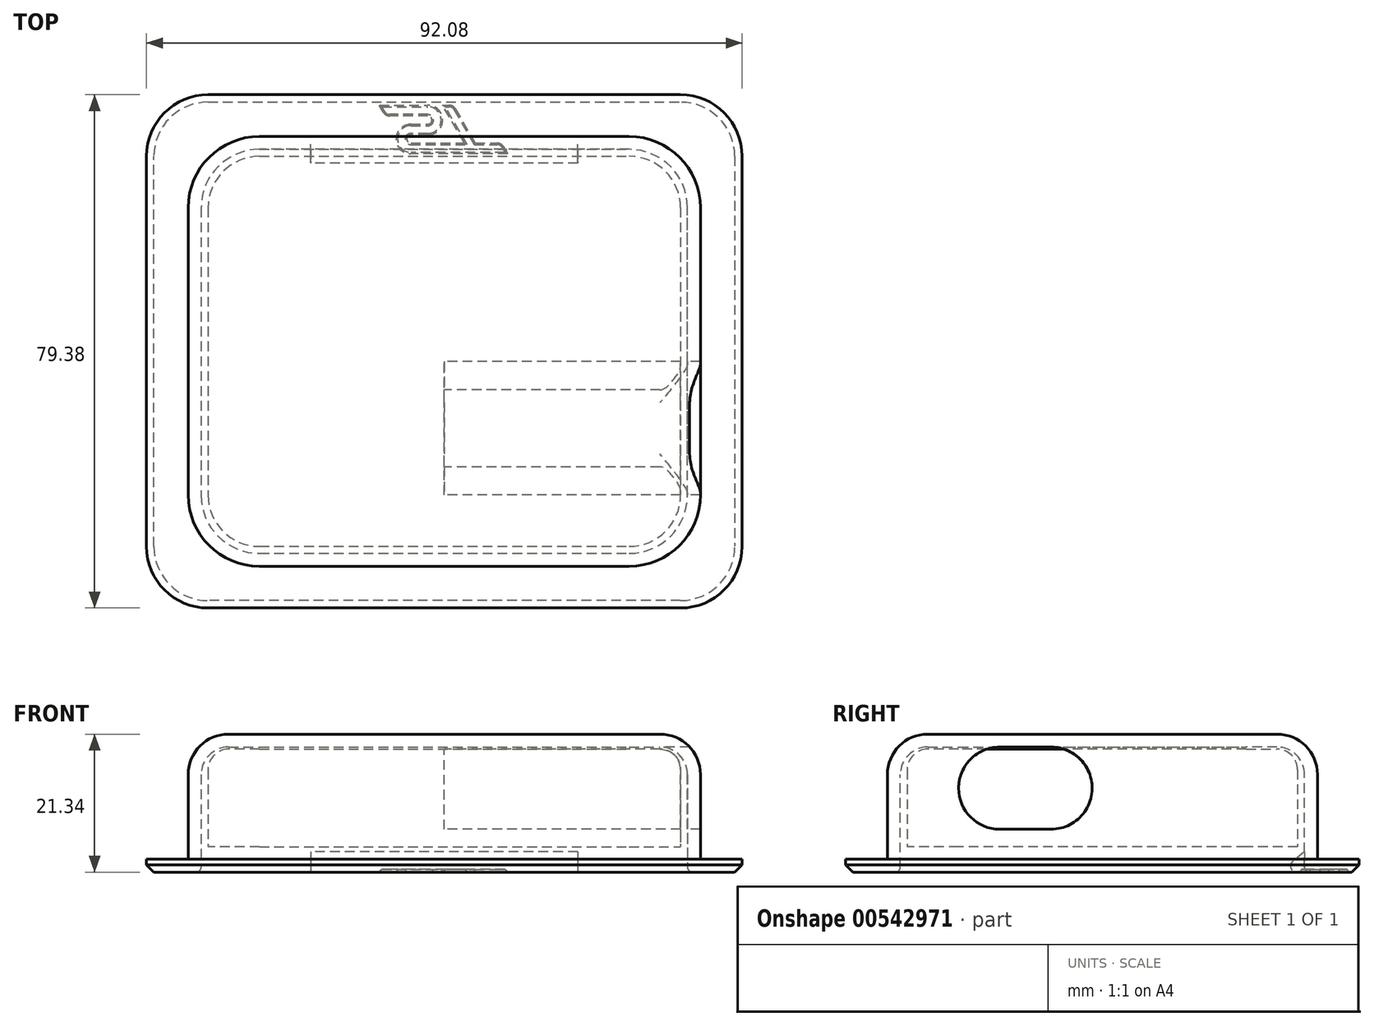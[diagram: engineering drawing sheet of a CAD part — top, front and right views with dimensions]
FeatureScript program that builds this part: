
annotation { "Feature Type Name" : "Feature", "Feature Type Description" : "" }
export const myFeature = defineFeature(function(context is Context, id is Id, definition is map)
    precondition{}
    {
        {
            var Q0;
            Q0=qCreatedBy(makeId("Top.planeOp"),FACE);
            var sketch = newSketch(context, id + "F0", { "sketchPlane" : qUnion([Q0])});
            skLineSegment(sketch, "E0.bottom", {"start": v(-28.58, 30.16) * mm, "end": v(28.58, 30.16) * mm});
            skLineSegment(sketch, "E0.top", {"start": v(-28.58, -30.16) * mm, "end": v(28.58, -30.16) * mm});
            skLineSegment(sketch, "E0.left", {"start": v(-36.51, 22.23) * mm, "end": v(-36.51, -22.23) * mm});
            skLineSegment(sketch, "E0.right", {"start": v(36.51, 22.23) * mm, "end": v(36.51, -22.23) * mm});
            skLineSegment(sketch, "E1", {"start": v(0, 30.16) * mm, "end": v(0, -30.16) * mm, "construction": true});
            skPoint(sketch, "E2.visualSharp", {"position": v(-36.51, 30.16) * mm});
            skArc(sketch, "E2.filletArc", {"start": v(-28.58, 30.16) * mm, "mid": v(-34.19, 27.84) * mm, "end": v(-36.51, 22.23) * mm});
            skPoint(sketch, "E3.visualSharp", {"position": v(-36.51, -30.16) * mm});
            skArc(sketch, "E3.filletArc", {"start": v(-36.51, -22.23) * mm, "mid": v(-34.19, -27.84) * mm, "end": v(-28.58, -30.16) * mm});
            skPoint(sketch, "E4.visualSharp", {"position": v(36.51, 30.16) * mm});
            skArc(sketch, "E4.filletArc", {"start": v(36.51, 22.23) * mm, "mid": v(34.19, 27.84) * mm, "end": v(28.58, 30.16) * mm});
            skPoint(sketch, "E5.visualSharp", {"position": v(36.51, -30.16) * mm});
            skArc(sketch, "E5.filletArc", {"start": v(28.58, -30.16) * mm, "mid": v(34.19, -27.84) * mm, "end": v(36.51, -22.22) * mm});
            skSolve(sketch);
        }
        {
            var Q0;
            Q0 = qSketchRegion(id + "F0", true);
            extrude(context, id + "F1", {"entities" : qUnion([Q0]), "depth" : 18.26 * mm, "offsetDistance" : 25.4 * mm});
        }
        {
            var Q0;
            Q0=makeQuery(id+"F1.opExtrude","CAP_EDGE",EDGE,{"disambiguationData":[OSD([sQuery(id+"F0.wireOp",EDGE,"E0.right")])],"isStart":true});
            var Q1;
            Q1=makeQuery(id+"F1.opExtrude","CAP_FACE",FACE,{"disambiguationData":[OSD([sQuery(id+"F0.wireOp",EDGE,"E0.bottom"),sQuery(id+"F0.wireOp",EDGE,"E0.top"),sQuery(id+"F0.wireOp",EDGE,"E0.left"),sQuery(id+"F0.wireOp",EDGE,"E0.right"),sQuery(id+"F0.wireOp",EDGE,"E2.filletArc"),sQuery(id+"F0.wireOp",EDGE,"E3.filletArc"),sQuery(id+"F0.wireOp",EDGE,"E4.filletArc"),sQuery(id+"F0.wireOp",EDGE,"E5.filletArc")])],"isStart":false});
            fillet(context, id + "F2", {"entities" : qUnion([Q0, Q1]), "radius" : 3.17 * mm, "tangentPropagation" : true, "allowEdgeOverflow" : false});
        }
        {
            var Q0;
            Q0=makeQuery(id+"F1.opExtrude","CAP_FACE",FACE,{"disambiguationData":[OSD([sQuery(id+"F0.wireOp",EDGE,"E0.bottom"),sQuery(id+"F0.wireOp",EDGE,"E0.top"),sQuery(id+"F0.wireOp",EDGE,"E0.left"),sQuery(id+"F0.wireOp",EDGE,"E0.right"),sQuery(id+"F0.wireOp",EDGE,"E2.filletArc"),sQuery(id+"F0.wireOp",EDGE,"E3.filletArc"),sQuery(id+"F0.wireOp",EDGE,"E4.filletArc"),sQuery(id+"F0.wireOp",EDGE,"E5.filletArc")])],"isStart":false});
            var sketch = newSketch(context, id + "F3", { "sketchPlane" : qUnion([Q0])});
            skCircle(sketch, "E6", {"center": v(0, 1.94) * mm, "radius": 1.78 * mm});
            skSolve(sketch);
        }
        {
            var Q0;
            Q0=qCreatedBy(makeId("Top.planeOp"),FACE);
            cPlane(context, id + "F4", {"entities" : qUnion([Q0]), "cplaneType" : CPlaneType.OFFSET, "offset" : 50.8 * mm, "width" : 152.4 * mm, "height" : 152.4 * mm});
        }
        {
            var Q0;
            Q0=qCreatedBy(id+"F4.planeOp",FACE);
            var sketch = newSketch(context, id + "F5", { "sketchPlane" : qUnion([Q0])});
            skLineSegment(sketch, "E7.bottom", {"start": v(-46.04, 39.69) * mm, "end": v(46.04, 39.69) * mm});
            skLineSegment(sketch, "E7.top", {"start": v(-46.04, -39.69) * mm, "end": v(46.04, -39.69) * mm});
            skLineSegment(sketch, "E7.left", {"start": v(-46.04, 39.69) * mm, "end": v(-46.04, -39.69) * mm});
            skLineSegment(sketch, "E7.right", {"start": v(46.04, 39.69) * mm, "end": v(46.04, -39.69) * mm});
            skLineSegment(sketch, "E8", {"start": v(0, 39.69) * mm, "end": v(0, -39.69) * mm, "construction": true});
            skLineSegment(sketch, "E9.0", {"start": v(-28.58, 30.16) * mm, "end": v(28.58, 30.16) * mm, "construction": true});
            skArc(sketch, "E9.1", {"start": v(28.58, 30.16) * mm, "mid": v(34.19, 27.84) * mm, "end": v(36.51, 22.23) * mm, "construction": true});
            skLineSegment(sketch, "E9.2", {"start": v(36.51, 22.23) * mm, "end": v(36.51, -22.23) * mm, "construction": true});
            skArc(sketch, "E9.3", {"start": v(36.51, -22.23) * mm, "mid": v(34.19, -27.84) * mm, "end": v(28.58, -30.16) * mm, "construction": true});
            skLineSegment(sketch, "E9.4", {"start": v(28.58, -30.16) * mm, "end": v(-28.58, -30.16) * mm, "construction": true});
            skArc(sketch, "E9.5", {"start": v(-28.58, -30.16) * mm, "mid": v(-34.19, -27.84) * mm, "end": v(-36.51, -22.23) * mm, "construction": true});
            skLineSegment(sketch, "E9.6", {"start": v(-36.51, -22.23) * mm, "end": v(-36.51, 22.23) * mm, "construction": true});
            skArc(sketch, "E9.7", {"start": v(-36.51, 22.23) * mm, "mid": v(-34.19, 27.84) * mm, "end": v(-28.58, 30.16) * mm, "construction": true});
            skSolve(sketch);
        }
        {
            var Q0;
            Q0 = qSketchRegion(id + "F5", true);
            extrude(context, id + "F6", {"entities" : qUnion([Q0]), "depth" : 22.22 * mm, "offsetDistance" : 25.4 * mm});
        }
        {
            var Q0;
            Q0=makeQuery(id+"F1.opExtrude","SWEPT_BODY",BODY,{"disambiguationData":[OSD([sQuery(id+"F0.wireOp",EDGE,"E0.bottom"),sQuery(id+"F0.wireOp",EDGE,"E0.top"),sQuery(id+"F0.wireOp",EDGE,"E0.left"),sQuery(id+"F0.wireOp",EDGE,"E0.right"),sQuery(id+"F0.wireOp",EDGE,"E2.filletArc"),sQuery(id+"F0.wireOp",EDGE,"E3.filletArc"),sQuery(id+"F0.wireOp",EDGE,"E4.filletArc"),sQuery(id+"F0.wireOp",EDGE,"E5.filletArc")])]});
            transform(context, id + "F7", {"entities" : qUnion([Q0]), "transformType" : TransformType.TRANSLATION_3D, "dx" : 0 * mm, "dy" : 0 * mm, "dz" : 50.8 * mm, "makeCopy" : false});
        }
        {
            var Q0;
            Q0=makeQuery(id+"F1.opExtrude","SWEPT_BODY",BODY,{"disambiguationData":[OSD([sQuery(id+"F0.wireOp",EDGE,"E0.bottom"),sQuery(id+"F0.wireOp",EDGE,"E0.top"),sQuery(id+"F0.wireOp",EDGE,"E0.left"),sQuery(id+"F0.wireOp",EDGE,"E0.right"),sQuery(id+"F0.wireOp",EDGE,"E2.filletArc"),sQuery(id+"F0.wireOp",EDGE,"E3.filletArc"),sQuery(id+"F0.wireOp",EDGE,"E4.filletArc"),sQuery(id+"F0.wireOp",EDGE,"E5.filletArc")])]});
            var Q1;
            Q1=makeQuery(id+"F6.opExtrude","SWEPT_BODY",BODY,{"disambiguationData":[OSD([sQuery(id+"F5.wireOp",EDGE,"E7.bottom"),sQuery(id+"F5.wireOp",EDGE,"E7.top"),sQuery(id+"F5.wireOp",EDGE,"E7.left"),sQuery(id+"F5.wireOp",EDGE,"E7.right")])]});
            booleanBodies(context, id + "F8", {"operationType" : BooleanOperationType.SUBTRACTION, "tools" : qUnion([Q0]), "targets" : qUnion([Q1]), "offset" : true, "offsetAll" : true, "offsetDistance" : 1.08 * mm, "keepTools" : true});
        }
        {
            var Q0;
            Q0=qCreatedBy(id+"F4.planeOp",FACE);
            var Q1;
            {var subQ0=sQuery(id+"F0.wireOp",EDGE,"E2.filletArc");var subQ1=sQuery(id+"F0.wireOp",EDGE,"E0.left");Q1=makeQuery(id+"F8.tempBoolean.opBoolean","COPY",VERTEX,{"derivedFrom":makeQuery(id+"F8.offsetTempBody.opPattern","COPY",VERTEX,{"derivedFrom":makeQuery(id+"F2.opFillet","BLEND_VERTEX",VERTEX,{"blendedFrom":[makeQuery(id+"F1.opExtrude","CAP_EDGE",EDGE,{"disambiguationData":[OSD([subQ1])],"isStart":true}),makeQuery(id+"F1.opExtrude","CAP_EDGE",EDGE,{"disambiguationData":[OSD([subQ0])],"isStart":true}),makeQuery(id+"F1.opExtrude","SWEPT_FACE",FACE,{"disambiguationData":[OSD([subQ1])]}),makeQuery(id+"F1.opExtrude","SWEPT_FACE",FACE,{"disambiguationData":[OSD([subQ0])]})],"blendedInto":[makeQuery(id+"F1.opExtrude","SWEPT_FACE",FACE,{"disambiguationData":[OSD([subQ1])]}),makeQuery(id+"F1.opExtrude","SWEPT_FACE",FACE,{"disambiguationData":[OSD([subQ0])]})]}),"instanceName":"1"})});}
            cPlane(context, id + "F9", {"entities" : qUnion([Q0, Q1]), "cplaneType" : CPlaneType.PLANE_POINT, "offset" : 25.4 * mm, "width" : 152.4 * mm, "height" : 152.4 * mm});
        }
        {
            var Q0;
            Q0=qCreatedBy(id+"F9.planeOp",FACE);
            var sketch = newSketch(context, id + "F10", { "sketchPlane" : qUnion([Q0])});
            skArc(sketch, "E10.0", {"start": v(28.58, -31.24) * mm, "mid": v(34.95, -28.6) * mm, "end": v(37.6, -22.22) * mm});
            skLineSegment(sketch, "E10.1", {"start": v(37.6, -22.22) * mm, "end": v(37.6, 22.23) * mm});
            skArc(sketch, "E10.2", {"start": v(37.6, 22.23) * mm, "mid": v(34.95, 28.6) * mm, "end": v(28.58, 31.24) * mm});
            skLineSegment(sketch, "E10.3", {"start": v(-28.58, -31.24) * mm, "end": v(28.58, -31.24) * mm});
            skLineSegment(sketch, "E10.4", {"start": v(28.58, 31.24) * mm, "end": v(-28.58, 31.24) * mm});
            skArc(sketch, "E10.5", {"start": v(-28.58, 31.24) * mm, "mid": v(-34.95, 28.6) * mm, "end": v(-37.6, 22.23) * mm});
            skLineSegment(sketch, "E10.6", {"start": v(-37.6, 22.23) * mm, "end": v(-37.6, -22.23) * mm});
            skArc(sketch, "E10.7", {"start": v(-37.6, -22.23) * mm, "mid": v(-34.95, -28.6) * mm, "end": v(-28.58, -31.24) * mm});
            skSolve(sketch);
        }
        {
            var Q0;
            Q0 = qSketchRegion(id + "F10", true);
            var Q1;
            Q1=makeQuery(id+"F6.opExtrude","CAP_FACE",FACE,{"disambiguationData":[OSD([sQuery(id+"F5.wireOp",EDGE,"E7.bottom"),sQuery(id+"F5.wireOp",EDGE,"E7.top"),sQuery(id+"F5.wireOp",EDGE,"E7.left"),sQuery(id+"F5.wireOp",EDGE,"E7.right")])],"isStart":true});
            extrude(context, id + "F11", {"entities" : qUnion([Q0]), "operationType" : NewBodyOperationType.REMOVE, "endBound" : BoundingType.THROUGH_ALL, "oppositeDirection" : true, "depth" : 25.4 * mm, "endBoundEntityFace" : qUnion([Q1]), "offsetDistance" : 25.4 * mm});
        }
        {
            var Q0;
            Q0=makeQuery(id+"F6.opExtrude","SWEPT_FACE",FACE,{"disambiguationData":[OSD([sQuery(id+"F5.wireOp",EDGE,"E7.bottom")])]});
            var Q1;
            Q1=makeQuery(id+"F6.opExtrude","CAP_FACE",FACE,{"disambiguationData":[OSD([sQuery(id+"F5.wireOp",EDGE,"E7.bottom"),sQuery(id+"F5.wireOp",EDGE,"E7.top"),sQuery(id+"F5.wireOp",EDGE,"E7.left"),sQuery(id+"F5.wireOp",EDGE,"E7.right")])],"isStart":false});
            var Q2;
            Q2=makeQuery(id+"F6.opExtrude","SWEPT_FACE",FACE,{"disambiguationData":[OSD([sQuery(id+"F5.wireOp",EDGE,"E7.left")])]});
            var Q3;
            Q3=makeQuery(id+"F6.opExtrude","SWEPT_FACE",FACE,{"disambiguationData":[OSD([sQuery(id+"F5.wireOp",EDGE,"E7.top")])]});
            var Q4;
            Q4=makeQuery(id+"F6.opExtrude","SWEPT_FACE",FACE,{"disambiguationData":[OSD([sQuery(id+"F5.wireOp",EDGE,"E7.right")])]});
            shell(context, id + "F12", {"entities" : qUnion([Q0, Q1, Q2, Q3, Q4]), "thickness" : 2 * mm});
        }
        {
            var Q0;
            Q0=makeQuery(id+"F20.opExtrude","CAP_EDGE",EDGE,{"disambiguationData":[OSD([sQuery(id+"F19.wireOp",EDGE,"3854df1f-5eea-4c8c-9dfc-7f40932c4ef70.MirrorCS")])],"isStart":true});
            var Q1;
            Q1=makeQuery(id+"F20.opExtrude","CAP_EDGE",EDGE,{"disambiguationData":[OSD([sQuery(id+"F19.wireOp",EDGE,"3854df1f-5eea-4c8c-9dfc-7f40932c4ef70.MirrorCS")])],"isStart":false});
            var Q2;
            Q2=makeQuery(id+"F20.opExtrude","CAP_EDGE",EDGE,{"disambiguationData":[OSD([sQuery(id+"F19.wireOp",EDGE,"E47")])],"isStart":false});
            var Q3;
            Q3=makeQuery(id+"F20.opExtrude","CAP_EDGE",EDGE,{"disambiguationData":[OSD([sQuery(id+"F19.wireOp",EDGE,"E47")])],"isStart":true});
            var Q4;
            {var subQ0=makeQuery(id+"F11.opExtrude","SWEPT_FACE",FACE,{"disambiguationData":[OSD([sQuery(id+"F10.wireOp",EDGE,"E10.3")])]});var subQ1=makeQuery(id+"F6.opExtrude","CAP_FACE",FACE,{"disambiguationData":[OSD([sQuery(id+"F5.wireOp",EDGE,"E7.bottom"),sQuery(id+"F5.wireOp",EDGE,"E7.top"),sQuery(id+"F5.wireOp",EDGE,"E7.left"),sQuery(id+"F5.wireOp",EDGE,"E7.right")])],"isStart":true});Q4=makeQuery(id+"F20.boolean.opBoolean","SPLIT",EDGE,{"disambiguationData":[TD([makeQuery(id+"F8.tempBoolean.opBoolean","COPY",FACE,{"derivedFrom":makeQuery(id+"F8.offsetTempBody.opPattern","COPY",FACE,{"derivedFrom":makeQuery(id+"F1.opExtrude","SWEPT_FACE",FACE,{"disambiguationData":[OSD([sQuery(id+"F0.wireOp",EDGE,"E3.filletArc")])]}),"instanceName":"1"})})])],"derivedFrom":makeQuery(id+"F11.boolean.opBoolean","INTERSECT",EDGE,{"derivedFrom":[subQ1,subQ0]})});}
            var Q5;
            Q5=makeQuery(id+"F11.boolean.opBoolean","INTERSECT",EDGE,{"derivedFrom":[makeQuery(id+"F6.opExtrude","CAP_FACE",FACE,{"disambiguationData":[OSD([sQuery(id+"F5.wireOp",EDGE,"E7.bottom"),sQuery(id+"F5.wireOp",EDGE,"E7.top"),sQuery(id+"F5.wireOp",EDGE,"E7.left"),sQuery(id+"F5.wireOp",EDGE,"E7.right")])],"isStart":true}),makeQuery(id+"F11.opExtrude","SWEPT_FACE",FACE,{"disambiguationData":[OSD([sQuery(id+"F10.wireOp",EDGE,"E10.7")])]})]});
            var Q6;
            Q6=makeQuery(id+"F11.boolean.opBoolean","INTERSECT",EDGE,{"derivedFrom":[makeQuery(id+"F6.opExtrude","CAP_FACE",FACE,{"disambiguationData":[OSD([sQuery(id+"F5.wireOp",EDGE,"E7.bottom"),sQuery(id+"F5.wireOp",EDGE,"E7.top"),sQuery(id+"F5.wireOp",EDGE,"E7.left"),sQuery(id+"F5.wireOp",EDGE,"E7.right")])],"isStart":true}),makeQuery(id+"F11.opExtrude","SWEPT_FACE",FACE,{"disambiguationData":[OSD([sQuery(id+"F10.wireOp",EDGE,"E10.0")])]})]});
            fillet(context, id + "F13", {"entities" : qUnion([Q0, Q1, Q2, Q3, Q4, Q5, Q6]), "radius" : 0.76 * mm, "tangentPropagation" : true, "allowEdgeOverflow" : false});
        }
        {
            var Q0;
            Q0=qCreatedBy(makeId("Front.planeOp"),FACE);
            var sketch = newSketch(context, id + "F14", { "sketchPlane" : qUnion([Q0])});
            skLineSegment(sketch, "E11.0", {"start": v(28.58, 70.14) * mm, "end": v(-28.58, 70.14) * mm, "construction": true});
            skLineSegment(sketch, "E12", {"start": v(0, 0) * mm, "end": v(0, 70.14) * mm, "construction": true});
            skLineSegment(sketch, "E13", {"start": v(3.97, 70.14) * mm, "end": v(-3.97, 70.14) * mm});
            skLineSegment(sketch, "E14", {"start": v(3.97, 57.44) * mm, "end": v(-3.97, 57.44) * mm});
            skArc(sketch, "E15", {"start": v(3.97, 57.44) * mm, "mid": v(10.32, 63.79) * mm, "end": v(3.97, 70.14) * mm});
            skArc(sketch, "E16", {"start": v(-3.97, 57.44) * mm, "mid": v(-10.32, 63.79) * mm, "end": v(-3.97, 70.14) * mm});
            skSolve(sketch);
        }
        {
            var Q0;
            Q0=makeQuery(id+"F6.opExtrude","SWEPT_EDGE",EDGE,{"disambiguationData":[OSD([sQuery(id+"F5.wireOp",EDGE,"E7.top"),sQuery(id+"F5.wireOp",EDGE,"E7.left")])]});
            var Q1;
            Q1=makeQuery(id+"F6.opExtrude","SWEPT_EDGE",EDGE,{"disambiguationData":[OSD([sQuery(id+"F5.wireOp",EDGE,"E7.bottom"),sQuery(id+"F5.wireOp",EDGE,"E7.left")])]});
            var Q2;
            Q2=makeQuery(id+"F6.opExtrude","SWEPT_EDGE",EDGE,{"disambiguationData":[OSD([sQuery(id+"F5.wireOp",EDGE,"E7.bottom"),sQuery(id+"F5.wireOp",EDGE,"E7.right")])]});
            var Q3;
            Q3=makeQuery(id+"F6.opExtrude","SWEPT_EDGE",EDGE,{"disambiguationData":[OSD([sQuery(id+"F5.wireOp",EDGE,"E7.top"),sQuery(id+"F5.wireOp",EDGE,"E7.right")])]});
            fillet(context, id + "F15", {"entities" : qUnion([Q0, Q1, Q2, Q3]), "radius" : 9.52 * mm, "tangentPropagation" : true, "allowEdgeOverflow" : false});
        }
        {
            var Q0;
            Q0=makeQuery(id+"F6.opExtrude","CAP_EDGE",EDGE,{"disambiguationData":[OSD([sQuery(id+"F5.wireOp",EDGE,"E7.left")])],"isStart":true});
            var Q1;
            Q1=makeQuery(id+"F6.opExtrude","CAP_EDGE",EDGE,{"disambiguationData":[OSD([sQuery(id+"F5.wireOp",EDGE,"E7.top")])],"isStart":true});
            var Q2;
            Q2=makeQuery(id+"F6.opExtrude","CAP_EDGE",EDGE,{"disambiguationData":[OSD([sQuery(id+"F5.wireOp",EDGE,"E7.right")])],"isStart":true});
            var Q3;
            Q3=makeQuery(id+"F6.opExtrude","CAP_EDGE",EDGE,{"disambiguationData":[OSD([sQuery(id+"F5.wireOp",EDGE,"E7.bottom")])],"isStart":true});
            chamfer(context, id + "F16", {"entities" : qUnion([Q0, Q1, Q2, Q3]), "width" : 1.14 * mm, "tangentPropagation" : true});
        }
        {
            var Q0;
            Q0=makeQuery(id+"F00SdX4fDEoqiSf_2.boolean.opBoolean","MERGE",FACE,{"derivedFrom":[makeQuery(id+"F8.tempBoolean.opBoolean","COPY",FACE,{"derivedFrom":makeQuery(id+"F8.offsetTempBody.opPattern","COPY",FACE,{"derivedFrom":makeQuery(id+"F1.opExtrude","CAP_FACE",FACE,{"disambiguationData":[OSD([sQuery(id+"F0.wireOp",EDGE,"E0.bottom"),sQuery(id+"F0.wireOp",EDGE,"E0.top"),sQuery(id+"F0.wireOp",EDGE,"E0.left"),sQuery(id+"F0.wireOp",EDGE,"E0.right"),sQuery(id+"F0.wireOp",EDGE,"E2.filletArc"),sQuery(id+"F0.wireOp",EDGE,"E3.filletArc"),sQuery(id+"F0.wireOp",EDGE,"E4.filletArc"),sQuery(id+"F0.wireOp",EDGE,"E5.filletArc")])],"isStart":false}),"instanceName":"1"})}),makeQuery(id+"F00SdX4fDEoqiSf_2.opExtrude","SWEPT_FACE",FACE,{"disambiguationData":[OSD([sQuery(id+"F14.wireOp",EDGE,"E13")])]})]});
            var sketch = newSketch(context, id + "F17", { "sketchPlane" : qUnion([Q0])});
            skLineSegment(sketch, "E17", {"start": v(16.14, 8.2) * mm, "end": v(-28.51, 8.2) * mm, "construction": true});
            skLineSegment(sketch, "E18", {"start": v(0, 26.99) * mm, "end": v(26.24, 26.99) * mm, "construction": true});
            skLineSegment(sketch, "E19.MirrorCS", {"start": v(28.51, -11.8) * mm, "end": v(-28.51, -11.8) * mm, "construction": true});
            skLineSegment(sketch, "E20", {"start": v(-28.51, -11.8) * mm, "end": v(16.03, -11.8) * mm});
            skLineSegment(sketch, "E21", {"start": v(16.03, -7.4) * mm, "end": v(-6.08, -7.4) * mm});
            skLineSegment(sketch, "E22", {"start": v(16.03, 0.4) * mm, "end": v(9.03, 0.4) * mm});
            skLineSegment(sketch, "E23", {"start": v(28.51, 8.2) * mm, "end": v(9.03, 8.2) * mm});
            skLineSegment(sketch, "E24", {"start": v(28.51, 8.2) * mm, "end": v(26.58, 4.85) * mm});
            skLineSegment(sketch, "E25", {"start": v(24.76, 3.8) * mm, "end": v(9.03, 3.8) * mm});
            skArc(sketch, "E26", {"start": v(9.03, 3.8) * mm, "mid": v(7.33, 2.1) * mm, "end": v(9.03, 0.4) * mm});
            skLineSegment(sketch, "E27", {"start": v(16.03, -4) * mm, "end": v(9.03, -4) * mm});
            skArc(sketch, "E28", {"start": v(16.03, -4) * mm, "mid": v(17.73, -5.7) * mm, "end": v(16.03, -7.4) * mm});
            skArc(sketch, "E29", {"start": v(16.03, 0.4) * mm, "mid": v(22.13, -5.7) * mm, "end": v(16.03, -11.8) * mm});
            skArc(sketch, "E30", {"start": v(9.03, -4) * mm, "mid": v(2.93, 2.1) * mm, "end": v(9.03, 8.2) * mm});
            skLineSegment(sketch, "E31", {"start": v(-6.08, -7.4) * mm, "end": v(2.93, 8.2) * mm});
            skLineSegment(sketch, "E32", {"start": v(2.93, 8.2) * mm, "end": v(-0.26, 8.2) * mm});
            skLineSegment(sketch, "E33", {"start": v(-2.07, 7.15) * mm, "end": v(-10.48, -7.4) * mm});
            skLineSegment(sketch, "E34", {"start": v(-10.48, -7.4) * mm, "end": v(-24.76, -7.4) * mm});
            skLineSegment(sketch, "E35", {"start": v(-26.58, -8.45) * mm, "end": v(-28.51, -11.8) * mm});
            skLineSegment(sketch, "E36", {"start": v(13.78, 26.99) * mm, "end": v(9.38, 26.99) * mm, "construction": true});
            skLineSegment(sketch, "E37", {"start": v(9.03, 0.4) * mm, "end": v(9.03, -4) * mm, "construction": true});
            skPoint(sketch, "E38", {"position": v(2.93, 2.1) * mm});
            skLineSegment(sketch, "E39", {"start": v(0, 26.99) * mm, "end": v(0, -31.57) * mm, "construction": true});
            skPoint(sketch, "E40.visualSharp", {"position": v(25.97, 3.8) * mm});
            skArc(sketch, "E40.filletArc", {"start": v(24.76, 3.8) * mm, "mid": v(25.8, 4.08) * mm, "end": v(26.58, 4.85) * mm});
            skPoint(sketch, "E41.visualSharp", {"position": v(-1.47, 8.2) * mm});
            skArc(sketch, "E41.filletArc", {"start": v(-0.26, 8.2) * mm, "mid": v(-1.3, 7.92) * mm, "end": v(-2.07, 7.15) * mm});
            skPoint(sketch, "E42.visualSharp", {"position": v(-25.97, -7.4) * mm});
            skArc(sketch, "E42.filletArc", {"start": v(-24.76, -7.4) * mm, "mid": v(-25.8, -7.68) * mm, "end": v(-26.58, -8.45) * mm});
            skLineSegment(sketch, "E43", {"start": v(28.51, 8.2) * mm, "end": v(28.51, -11.8) * mm, "construction": true});
            skLineSegment(sketch, "E44", {"start": v(-28.51, -11.8) * mm, "end": v(-28.51, 8.2) * mm, "construction": true});
            skSolve(sketch);
        }
        {
            var Q0;
            Q0=makeQuery(id+"F1.opExtrude","SWEPT_BODY",BODY,{"disambiguationData":[OSD([sQuery(id+"F0.wireOp",EDGE,"E0.bottom"),sQuery(id+"F0.wireOp",EDGE,"E0.top"),sQuery(id+"F0.wireOp",EDGE,"E0.left"),sQuery(id+"F0.wireOp",EDGE,"E0.right"),sQuery(id+"F0.wireOp",EDGE,"E2.filletArc"),sQuery(id+"F0.wireOp",EDGE,"E3.filletArc"),sQuery(id+"F0.wireOp",EDGE,"E4.filletArc"),sQuery(id+"F0.wireOp",EDGE,"E5.filletArc")])]});
            transform(context, id + "F18", {"entities" : qUnion([Q0]), "transformType" : TransformType.TRANSLATION_3D, "dx" : 0 * mm, "dy" : 0 * mm, "dz" : 0.76 * mm, "makeCopy" : false});
        }
        {
            var Q0;
            Q0=qCreatedBy(makeId("Right.planeOp"),FACE);
            var sketch = newSketch(context, id + "F19", { "sketchPlane" : qUnion([Q0])});
            skPoint(sketch, "E45.0", {"position": v(31.24, 50.8) * mm});
            skLineSegment(sketch, "E46", {"start": v(31.24, 50.8) * mm, "end": v(31.24, 53) * mm, "construction": true});
            skArc(sketch, "E47", {"start": v(31.24, 53) * mm, "mid": v(30.64, 51.9) * mm, "end": v(31.24, 50.8) * mm, "construction": true});
            skLineSegment(sketch, "E48", {"start": v(0, 0) * mm, "end": v(0, 28.74) * mm, "construction": true});
            skArc(sketch, "E49.0", {"start": v(30.16, 54.74) * mm, "mid": v(29.23, 52.5) * mm, "end": v(26.99, 51.56) * mm, "construction": true});
            skLineSegment(sketch, "E50.0", {"start": v(-30.16, 66.64) * mm, "end": v(-30.16, 54.74) * mm, "construction": true});
            skLineSegment(sketch, "E50.2", {"start": v(30.16, 66.64) * mm, "end": v(30.16, 54.74) * mm, "construction": true});
            skArc(sketch, "E50.3", {"start": v(30.16, 54.74) * mm, "mid": v(29.23, 52.5) * mm, "end": v(26.99, 51.56) * mm});
            skLineSegment(sketch, "E51", {"start": v(31.24, 53.98) * mm, "end": v(29.42, 52.44) * mm});
            skLineSegment(sketch, "E52", {"start": v(31.24, 53.98) * mm, "end": v(31.24, 50.8) * mm});
            skLineSegment(sketch, "E53", {"start": v(30.01, 50.8) * mm, "end": v(31.24, 50.8) * mm});
            skArc(sketch, "E54", {"start": v(30.01, 50.8) * mm, "mid": v(29.14, 51.41) * mm, "end": v(29.42, 52.44) * mm});
            skArc(sketch, "E55.MirrorCS", {"start": v(32.47, 50.8) * mm, "mid": v(33.34, 51.41) * mm, "end": v(33.07, 52.44) * mm});
            skLineSegment(sketch, "E56.MirrorCS", {"start": v(32.47, 50.8) * mm, "end": v(31.24, 50.8) * mm});
            skArc(sketch, "E57.MirrorCS", {"start": v(32.32, 54.74) * mm, "mid": v(33.25, 52.5) * mm, "end": v(35.5, 51.56) * mm});
            skArc(sketch, "E58.MirrorCS", {"start": v(32.32, 54.74) * mm, "mid": v(33.25, 52.5) * mm, "end": v(35.5, 51.56) * mm, "construction": true});
            skLineSegment(sketch, "E59.MirrorCS", {"start": v(31.24, 53.98) * mm, "end": v(33.07, 52.44) * mm});
            skArc(sketch, "E60.MirrorCS", {"start": v(31.24, 53) * mm, "mid": v(31.85, 51.9) * mm, "end": v(31.24, 50.8) * mm, "construction": true});
            skPoint(sketch, "E61", {"position": v(32, 50.8) * mm});
            skPoint(sketch, "E62.MirrorP", {"position": v(30.48, 50.8) * mm});
            skLineSegment(sketch, "E63.MirrorCS", {"start": v(-32.47, 50.8) * mm, "end": v(-31.24, 50.8) * mm, "construction": true});
            skLineSegment(sketch, "E64.MirrorCS", {"start": v(-31.24, 53.98) * mm, "end": v(-31.24, 50.8) * mm, "construction": true});
            skArc(sketch, "E65.MirrorCS", {"start": v(-31.24, 53) * mm, "mid": v(-30.64, 51.9) * mm, "end": v(-31.24, 50.8) * mm, "construction": true});
            skArc(sketch, "E66.MirrorCS", {"start": v(-31.24, 53) * mm, "mid": v(-31.85, 51.9) * mm, "end": v(-31.24, 50.8) * mm, "construction": true});
            skLineSegment(sketch, "E67.MirrorCS", {"start": v(-30.01, 50.8) * mm, "end": v(-31.24, 50.8) * mm, "construction": true});
            skLineSegment(sketch, "E68.MirrorCS", {"start": v(-31.24, 50.8) * mm, "end": v(-31.24, 53) * mm, "construction": true});
            skPoint(sketch, "E69.MirrorP", {"position": v(-31.24, 50.8) * mm});
            skLineSegment(sketch, "E70.MirrorCS", {"start": v(-31.24, 53.98) * mm, "end": v(-33.07, 52.44) * mm});
            skLineSegment(sketch, "E71.MirrorCS", {"start": v(-31.24, 53.98) * mm, "end": v(-29.42, 52.44) * mm, "construction": true});
            skArc(sketch, "E72.MirrorCS", {"start": v(-30.16, 54.74) * mm, "mid": v(-29.23, 52.5) * mm, "end": v(-26.99, 51.56) * mm});
            skArc(sketch, "E73.MirrorCS", {"start": v(-32.32, 54.74) * mm, "mid": v(-33.25, 52.5) * mm, "end": v(-35.5, 51.56) * mm});
            skArc(sketch, "E74.MirrorCS", {"start": v(-32.47, 50.8) * mm, "mid": v(-33.34, 51.41) * mm, "end": v(-33.07, 52.44) * mm});
            skArc(sketch, "E75.MirrorCS", {"start": v(-30.01, 50.8) * mm, "mid": v(-29.14, 51.41) * mm, "end": v(-29.42, 52.44) * mm, "construction": true});
            skArc(sketch, "E76.MirrorCS", {"start": v(-30.16, 54.74) * mm, "mid": v(-29.23, 52.5) * mm, "end": v(-26.99, 51.56) * mm, "construction": true});
            skArc(sketch, "E77.MirrorCS", {"start": v(-32.32, 54.74) * mm, "mid": v(-33.25, 52.5) * mm, "end": v(-35.5, 51.56) * mm, "construction": true});
            skPoint(sketch, "E78.MirrorP", {"position": v(-30.48, 50.8) * mm});
            skPoint(sketch, "E79.MirrorP", {"position": v(-32, 50.8) * mm});
            skSolve(sketch);
        }
        {
            var Q0;
            Q0 = qSketchRegion(id + "F19", true);
            extrude(context, id + "F20", {"entities" : qUnion([Q0]), "operationType" : NewBodyOperationType.ADD, "depth" : 41.27 * mm, "offsetDistance" : 25.4 * mm, "symmetric" : true});
        }
        {
            var Q0;
            Q0=qCreatedBy(makeId("Right.planeOp"),FACE);
            var sketch = newSketch(context, id + "F21", { "sketchPlane" : qUnion([Q0])});
            skLineSegment(sketch, "E80.0", {"start": v(22.23, 70.14) * mm, "end": v(-26.99, 70.14) * mm, "construction": true});
            skLineSegment(sketch, "E81", {"start": v(-11.9, 18.42) * mm, "end": v(-11.9, 70.14) * mm, "construction": true});
            skLineSegment(sketch, "E82", {"start": v(-7.94, 70.14) * mm, "end": v(-15.88, 70.14) * mm});
            skLineSegment(sketch, "E83", {"start": v(-7.94, 57.44) * mm, "end": v(-15.88, 57.44) * mm});
            skArc(sketch, "E84", {"start": v(-7.94, 57.44) * mm, "mid": v(-1.59, 63.79) * mm, "end": v(-7.94, 70.14) * mm});
            skArc(sketch, "E85", {"start": v(-15.88, 57.44) * mm, "mid": v(-22.23, 63.79) * mm, "end": v(-15.88, 70.14) * mm});
            skLineSegment(sketch, "E86.0", {"start": v(-22.22, 65.88) * mm, "end": v(-22.22, 51.56) * mm, "construction": true});
            skSolve(sketch);
        }
        {
            var Q0;
            Q0 = qSketchRegion(id + "F21", true);
            extrude(context, id + "F22", {"entities" : qUnion([Q0]), "operationType" : NewBodyOperationType.REMOVE, "endBound" : BoundingType.THROUGH_ALL, "depth" : 25 * mm, "offsetDistance" : 25 * mm});
        }
        {
            var Q0;
            Q0=makeQuery(id+"F22.boolean.opBoolean","MERGE",FACE,{"derivedFrom":[makeQuery(id+"F8.tempBoolean.opBoolean","COPY",FACE,{"derivedFrom":makeQuery(id+"F8.offsetTempBody.opPattern","COPY",FACE,{"derivedFrom":makeQuery(id+"F1.opExtrude","CAP_FACE",FACE,{"disambiguationData":[OSD([sQuery(id+"F0.wireOp",EDGE,"E0.bottom"),sQuery(id+"F0.wireOp",EDGE,"E0.top"),sQuery(id+"F0.wireOp",EDGE,"E0.left"),sQuery(id+"F0.wireOp",EDGE,"E0.right"),sQuery(id+"F0.wireOp",EDGE,"E2.filletArc"),sQuery(id+"F0.wireOp",EDGE,"E3.filletArc"),sQuery(id+"F0.wireOp",EDGE,"E4.filletArc"),sQuery(id+"F0.wireOp",EDGE,"E5.filletArc")])],"isStart":false}),"instanceName":"1"})})],"fromTools":[makeQuery(id+"F22.opExtrude","SWEPT_FACE",FACE,{"disambiguationData":[OSD([sQuery(id+"F21.wireOp",EDGE,"E82")])]})]});
            var sketch = newSketch(context, id + "F23", { "sketchPlane" : qUnion([Q0])});
            skLineSegment(sketch, "E87", {"start": v(-114.92, -8.36) * mm, "end": v(27.72, -8.36) * mm, "construction": true});
            skLineSegment(sketch, "E88", {"start": v(-0.78, -126.94) * mm, "end": v(-125.02, -126.94) * mm, "construction": true});
            skLineSegment(sketch, "E89.MirrorCS", {"start": v(-29.28, 11.64) * mm, "end": v(27.72, 11.64) * mm, "construction": true});
            skLineSegment(sketch, "E90", {"start": v(27.72, 11.64) * mm, "end": v(-16.78, 11.64) * mm});
            skLineSegment(sketch, "E91", {"start": v(-16.78, 7.25) * mm, "end": v(5.32, 7.25) * mm});
            skLineSegment(sketch, "E92", {"start": v(-16.78, -0.55) * mm, "end": v(-9.78, -0.55) * mm});
            skLineSegment(sketch, "E93", {"start": v(-29.28, -8.36) * mm, "end": v(-9.78, -8.36) * mm});
            skLineSegment(sketch, "E94", {"start": v(-29.28, -8.36) * mm, "end": v(-27.35, -5) * mm});
            skLineSegment(sketch, "E95", {"start": v(-25.53, -3.96) * mm, "end": v(-9.78, -3.96) * mm});
            skArc(sketch, "E96", {"start": v(-9.78, -3.96) * mm, "mid": v(-8.08, -2.26) * mm, "end": v(-9.78, -0.55) * mm});
            skLineSegment(sketch, "E97", {"start": v(-16.78, 3.84) * mm, "end": v(-9.78, 3.84) * mm});
            skArc(sketch, "E98", {"start": v(-16.78, 3.84) * mm, "mid": v(-18.48, 5.54) * mm, "end": v(-16.78, 7.25) * mm});
            skArc(sketch, "E99", {"start": v(-16.78, -0.55) * mm, "mid": v(-22.88, 5.54) * mm, "end": v(-16.78, 11.64) * mm});
            skArc(sketch, "E100", {"start": v(-9.78, 3.84) * mm, "mid": v(-3.68, -2.26) * mm, "end": v(-9.78, -8.36) * mm});
            skLineSegment(sketch, "E101", {"start": v(5.32, 7.25) * mm, "end": v(-3.68, -8.36) * mm});
            skLineSegment(sketch, "E102", {"start": v(-3.68, -8.36) * mm, "end": v(-0.5, -8.36) * mm});
            skLineSegment(sketch, "E103", {"start": v(1.32, -7.3) * mm, "end": v(9.72, 7.25) * mm});
            skLineSegment(sketch, "E104", {"start": v(9.72, 7.25) * mm, "end": v(23.97, 7.25) * mm});
            skLineSegment(sketch, "E105", {"start": v(25.78, 8.3) * mm, "end": v(27.72, 11.64) * mm});
            skLineSegment(sketch, "E106", {"start": v(-72.15, -126.94) * mm, "end": v(-67.75, -126.94) * mm, "construction": true});
            skLineSegment(sketch, "E107", {"start": v(-9.78, -0.55) * mm, "end": v(-9.78, 3.84) * mm, "construction": true});
            skPoint(sketch, "E108", {"position": v(-3.68, -2.26) * mm});
            skLineSegment(sketch, "E109", {"start": v(-0.78, -126.94) * mm, "end": v(-0.78, -43.74) * mm, "construction": true});
            skPoint(sketch, "E110.visualSharp", {"position": v(-26.74, -3.96) * mm});
            skArc(sketch, "E110.filletArc", {"start": v(-25.53, -3.96) * mm, "mid": v(-26.58, -4.24) * mm, "end": v(-27.35, -5) * mm});
            skPoint(sketch, "E111.visualSharp", {"position": v(0.71, -8.36) * mm});
            skArc(sketch, "E111.filletArc", {"start": v(-0.5, -8.36) * mm, "mid": v(0.55, -8.07) * mm, "end": v(1.32, -7.3) * mm});
            skPoint(sketch, "E112.visualSharp", {"position": v(25.18, 7.25) * mm});
            skArc(sketch, "E112.filletArc", {"start": v(23.97, 7.25) * mm, "mid": v(25.02, 7.53) * mm, "end": v(25.78, 8.3) * mm});
            skLineSegment(sketch, "E113", {"start": v(-29.28, -8.36) * mm, "end": v(-29.28, 11.64) * mm, "construction": true});
            skLineSegment(sketch, "E114", {"start": v(27.72, 11.64) * mm, "end": v(27.72, -8.36) * mm, "construction": true});
            skSolve(sketch);
        }
        {
            var Q0;
            {var subQ0=sQuery(id+"F19.wireOp",EDGE,"E56.MirrorCS");var subQ1=sQuery(id+"F19.wireOp",EDGE,"E53");Q0=makeQuery(id+"FQDNSK62ib1KjXu_2.1.F20.boolean.opBoolean","MERGE",FACE,{"derivedFrom":[makeQuery(id+"F20.boolean.opBoolean","MERGE",FACE,{"derivedFrom":[makeQuery(id+"F6.opExtrude","CAP_FACE",FACE,{"disambiguationData":[OSD([sQuery(id+"F5.wireOp",EDGE,"E7.bottom"),sQuery(id+"F5.wireOp",EDGE,"E7.top"),sQuery(id+"F5.wireOp",EDGE,"E7.left"),sQuery(id+"F5.wireOp",EDGE,"E7.right")])],"isStart":true}),makeQuery(id+"F20.opExtrude","SWEPT_FACE",FACE,{"disambiguationData":[OSD([subQ1,subQ0])]})]}),makeQuery(id+"FQDNSK62ib1KjXu_2.1.F20.opExtrude","SWEPT_FACE",FACE,{"disambiguationData":[OSD([subQ1,subQ0])]})]});}
            var sketch = newSketch(context, id + "F24", { "sketchPlane" : qUnion([Q0])});
            skLineSegment(sketch, "E115", {"start": v(-9.7, -38.06) * mm, "end": v(16.74, -38.06) * mm, "construction": true});
            skLineSegment(sketch, "E116", {"start": v(2.66, -35.62) * mm, "end": v(-14.74, -35.62) * mm, "construction": true});
            skLineSegment(sketch, "E117.MirrorCS", {"start": v(-9.7, -30.56) * mm, "end": v(9.78, -30.56) * mm, "construction": true});
            skLineSegment(sketch, "E118", {"start": v(9.78, -30.56) * mm, "end": v(-5.17, -30.56) * mm});
            skLineSegment(sketch, "E119", {"start": v(-5.17, -32.2) * mm, "end": v(3.12, -32.2) * mm});
            skLineSegment(sketch, "E120", {"start": v(-5.17, -35.13) * mm, "end": v(-2.54, -35.13) * mm});
            skLineSegment(sketch, "E121", {"start": v(-10.04, -38.06) * mm, "end": v(-2.54, -38.06) * mm});
            skLineSegment(sketch, "E122", {"start": v(-10.04, -38.06) * mm, "end": v(-9.41, -36.97) * mm});
            skLineSegment(sketch, "E123", {"start": v(-8.44, -36.4) * mm, "end": v(-2.54, -36.4) * mm});
            skArc(sketch, "E124", {"start": v(-2.54, -36.4) * mm, "mid": v(-1.9, -35.77) * mm, "end": v(-2.54, -35.13) * mm});
            skLineSegment(sketch, "E125", {"start": v(-5.17, -33.48) * mm, "end": v(-2.54, -33.48) * mm});
            skArc(sketch, "E126", {"start": v(-5.17, -33.48) * mm, "mid": v(-5.8, -32.84) * mm, "end": v(-5.17, -32.2) * mm});
            skArc(sketch, "E127", {"start": v(-5.17, -35.13) * mm, "mid": v(-7.45, -32.84) * mm, "end": v(-5.17, -30.56) * mm});
            skArc(sketch, "E128", {"start": v(-2.54, -33.48) * mm, "mid": v(-0.25, -35.77) * mm, "end": v(-2.54, -38.06) * mm});
            skLineSegment(sketch, "E129", {"start": v(3.12, -32.2) * mm, "end": v(-0.25, -38.06) * mm});
            skLineSegment(sketch, "E130", {"start": v(-0.25, -38.06) * mm, "end": v(0.75, -38.06) * mm});
            skLineSegment(sketch, "E131", {"start": v(1.72, -37.5) * mm, "end": v(4.77, -32.2) * mm});
            skLineSegment(sketch, "E132", {"start": v(4.77, -32.2) * mm, "end": v(8.17, -32.2) * mm});
            skLineSegment(sketch, "E133", {"start": v(9.15, -31.64) * mm, "end": v(9.78, -30.56) * mm});
            skLineSegment(sketch, "E134", {"start": v(2.1, -33.96) * mm, "end": v(3.76, -33.96) * mm, "construction": true});
            skLineSegment(sketch, "E135", {"start": v(-2.54, -35.13) * mm, "end": v(-2.54, -33.48) * mm, "construction": true});
            skPoint(sketch, "E136", {"position": v(-0.25, -35.77) * mm});
            skPoint(sketch, "E137.visualSharp", {"position": v(-9.09, -36.4) * mm});
            skArc(sketch, "E137.filletArc", {"start": v(-8.44, -36.4) * mm, "mid": v(-9, -36.56) * mm, "end": v(-9.41, -36.97) * mm});
            skPoint(sketch, "E138.visualSharp", {"position": v(1.4, -38.06) * mm});
            skArc(sketch, "E138.filletArc", {"start": v(0.75, -38.06) * mm, "mid": v(1.3, -37.9) * mm, "end": v(1.72, -37.5) * mm});
            skPoint(sketch, "E139.visualSharp", {"position": v(8.82, -32.2) * mm});
            skArc(sketch, "E139.filletArc", {"start": v(8.17, -32.2) * mm, "mid": v(8.74, -32.05) * mm, "end": v(9.15, -31.64) * mm});
            skSolve(sketch);
        }
        {
            var Q0;
            Q0 = qSketchRegion(id + "F24", true);
            extrude(context, id + "F25", {"entities" : qUnion([Q0]), "operationType" : NewBodyOperationType.REMOVE, "oppositeDirection" : true, "depth" : 0.4 * mm, "offsetDistance" : 25 * mm, "hasDraft" : true, "draftAngle" : 30 * degree, "draftPullDirection" : true});
        }
    });
